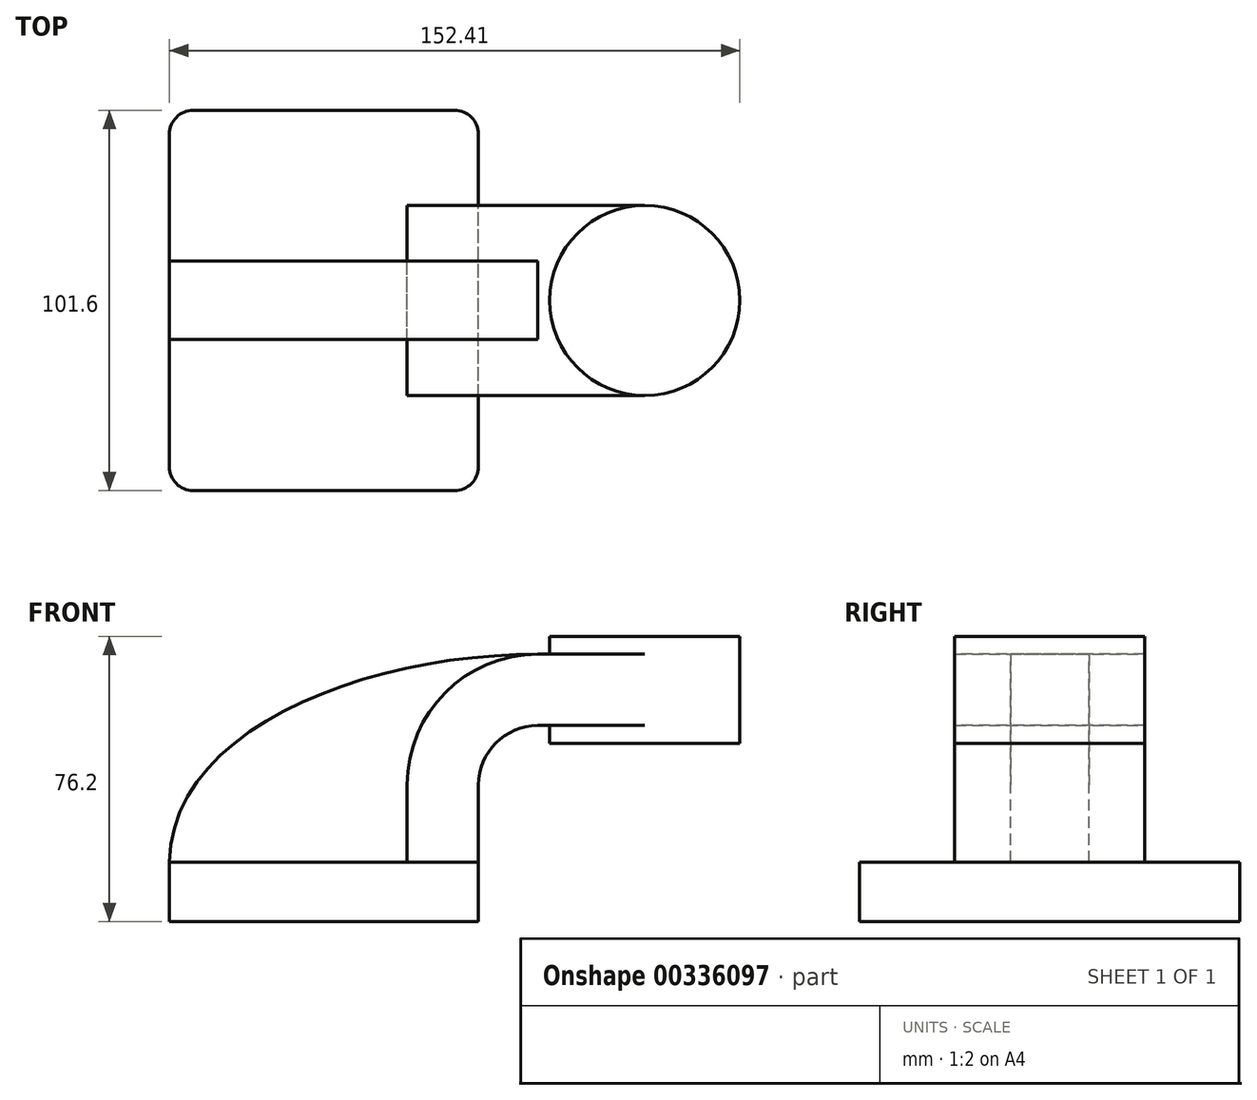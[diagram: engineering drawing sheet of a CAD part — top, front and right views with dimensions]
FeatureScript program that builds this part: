
annotation { "Feature Type Name" : "Feature", "Feature Type Description" : "" }
export const myFeature = defineFeature(function(context is Context, id is Id, definition is map)
    precondition{}
    {
        {
            var Q0;
            Q0=qCreatedBy(makeId("Front.planeOp"),FACE);
            var sketch = newSketch(context, id + "F0", { "sketchPlane" : qUnion([Q0])});
            skLineSegment(sketch, "E0.bottom", {"start": v(-41.27, -7.94) * mm, "end": v(41.28, -7.94) * mm});
            skLineSegment(sketch, "E0.top", {"start": v(-41.28, 7.94) * mm, "end": v(41.27, 7.94) * mm});
            skLineSegment(sketch, "E0.left", {"start": v(-41.27, -7.94) * mm, "end": v(-41.28, 7.94) * mm});
            skLineSegment(sketch, "E0.right", {"start": v(41.28, -7.94) * mm, "end": v(41.28, 7.94) * mm});
            skLineSegment(sketch, "E1", {"start": v(41.27, 7.94) * mm, "end": v(41.27, 28.59) * mm});
            skArc(sketch, "E2", {"start": v(57.15, 44.46) * mm, "mid": v(45.92, 39.81) * mm, "end": v(41.27, 28.59) * mm});
            skLineSegment(sketch, "E3", {"start": v(57.15, 44.46) * mm, "end": v(85.72, 44.46) * mm});
            skLineSegment(sketch, "E4.bottom", {"start": v(60.33, 39.69) * mm, "end": v(111.13, 39.69) * mm});
            skLineSegment(sketch, "E4.top", {"start": v(60.33, 68.26) * mm, "end": v(111.12, 68.26) * mm});
            skLineSegment(sketch, "E4.left", {"start": v(60.33, 39.69) * mm, "end": v(60.33, 68.26) * mm});
            skLineSegment(sketch, "E4.right", {"start": v(111.13, 39.69) * mm, "end": v(111.12, 68.26) * mm});
            skPoint(sketch, "E4.middle", {"position": v(85.73, 53.98) * mm});
            skLineSegment(sketch, "E5", {"start": v(-41.27, -7.94) * mm, "end": v(41.27, 7.94) * mm, "construction": true});
            skLineSegment(sketch, "E6", {"start": v(85.72, 68.26) * mm, "end": v(85.72, 39.69) * mm});
            skLineSegment(sketch, "E7", {"start": v(22.23, 7.94) * mm, "end": v(22.23, 28.59) * mm});
            skArc(sketch, "E8", {"start": v(57.15, 63.51) * mm, "mid": v(32.45, 53.28) * mm, "end": v(22.23, 28.59) * mm});
            skLineSegment(sketch, "E9", {"start": v(57.15, 63.51) * mm, "end": v(85.73, 63.51) * mm});
            skFitSpline(sketch, "E10", {"points": [v(-41.28, 7.94) * mm, v(57.15, 63.51) * mm], "startDerivative": vector(1.72, 110.1) * mm, "endDerivative": vector(131.6, -0.49) * mm});
            skSolve(sketch);
        }
        {
            var Q0;
            Q0=makeQuery(id+"F0.imprint","IMPRINT",FACE,{"disambiguationData":[TD([[makeQuery(id+"F0.imprint","IMPRINT",EDGE,{"derivedFrom":sQuery(id+"F0.wireOp",EDGE,"E0.bottom")}),1.0]])]});
            extrude(context, id + "F1", {"entities" : qUnion([Q0]), "depth" : 50.8 * mm, "hasSecondDirection" : true, "secondDirectionOppositeDirection" : true, "secondDirectionDepth" : 50.8 * mm});
        }
        {
            var Q0;
            {var subQ1=sQuery(id+"F0.wireOp",EDGE,"E1");Q0=makeQuery(id+"F0.imprint","IMPRINT",FACE,{"disambiguationData":[TD([[makeQuery(id+"F0.imprint","IMPRINT",EDGE,{"derivedFrom":subQ1}),1.0]])]});}
            var Q1;
            {var subQ0=sQuery(id+"F0.wireOp",EDGE,"E6");var subQ1=sQuery(id+"F0.wireOp",EDGE,"E3");var subQ2=makeQuery(id+"F0.imprint","INTERSECT",VERTEX,{"derivedFrom":[subQ1,subQ0]});Q1=makeQuery(id+"F0.imprint","IMPRINT",FACE,{"disambiguationData":[TD([[makeQuery(id+"F0.imprint","IMPRINT",EDGE,{"disambiguationData":[TD([[subQ2,1.0]])],"derivedFrom":subQ1}),1.0]])]});}
            extrude(context, id + "F2", {"entities" : qUnion([Q0, Q1]), "endBound" : BoundingType.SYMMETRIC, "offsetDistance" : 25.4 * mm, "depth" : 50.8 * mm});
        }
        {
            var Q0;
            {var subQ2=sQuery(id+"F0.wireOp",EDGE,"E7");Q0=makeQuery(id+"F0.imprint","IMPRINT",FACE,{"disambiguationData":[TD([[makeQuery(id+"F0.imprint","IMPRINT",EDGE,{"derivedFrom":subQ2}),1.0]])]});}
            extrude(context, id + "F3", {"entities" : qUnion([Q0]), "endBound" : BoundingType.SYMMETRIC, "depth" : 20.95 * mm, "offsetDistance" : 25.4 * mm});
        }
        {
            var Q0;
            {var subQ0=sQuery(id+"F0.wireOp",EDGE,"E4.right");Q0=makeQuery(id+"F0.imprint","IMPRINT",FACE,{"disambiguationData":[TD([[makeQuery(id+"F0.imprint","IMPRINT",EDGE,{"derivedFrom":subQ0}),1.0]])]});}
            var Q1;
            Q1=sQuery(id+"F0.wireOp",EDGE,"E6");
            revolve(context, id + "F4", {"operationType" : NewBodyOperationType.ADD, "surfaceOperationType" : NewSurfaceOperationType.NEW, "entities" : qUnion([Q0]), "axis" : qUnion([Q1]), "revolveType" : RevolveType.FULL});
        }
        {
            var Q0;
            Q0=makeQuery(id+"F1.opExtrude","CAP_EDGE",EDGE,{"disambiguationData":[OSD([sQuery(id+"F0.wireOp",EDGE,"E0.right")])],"isStart":false});
            var Q1;
            Q1=makeQuery(id+"F1.opExtrude","CAP_EDGE",EDGE,{"disambiguationData":[OSD([sQuery(id+"F0.wireOp",EDGE,"E0.left")])],"isStart":false});
            var Q2;
            Q2=makeQuery(id+"F1.opExtrude","CAP_EDGE",EDGE,{"disambiguationData":[OSD([sQuery(id+"F0.wireOp",EDGE,"E0.left")])],"isStart":true});
            var Q3;
            Q3=makeQuery(id+"F1.opExtrude","CAP_EDGE",EDGE,{"disambiguationData":[OSD([sQuery(id+"F0.wireOp",EDGE,"E0.right")])],"isStart":true});
            fillet(context, id + "F5", {"entities" : qUnion([Q0, Q1, Q2, Q3]), "radius" : 6.35 * mm, "tangentPropagation" : true, "allowEdgeOverflow" : false});
        }
    });
